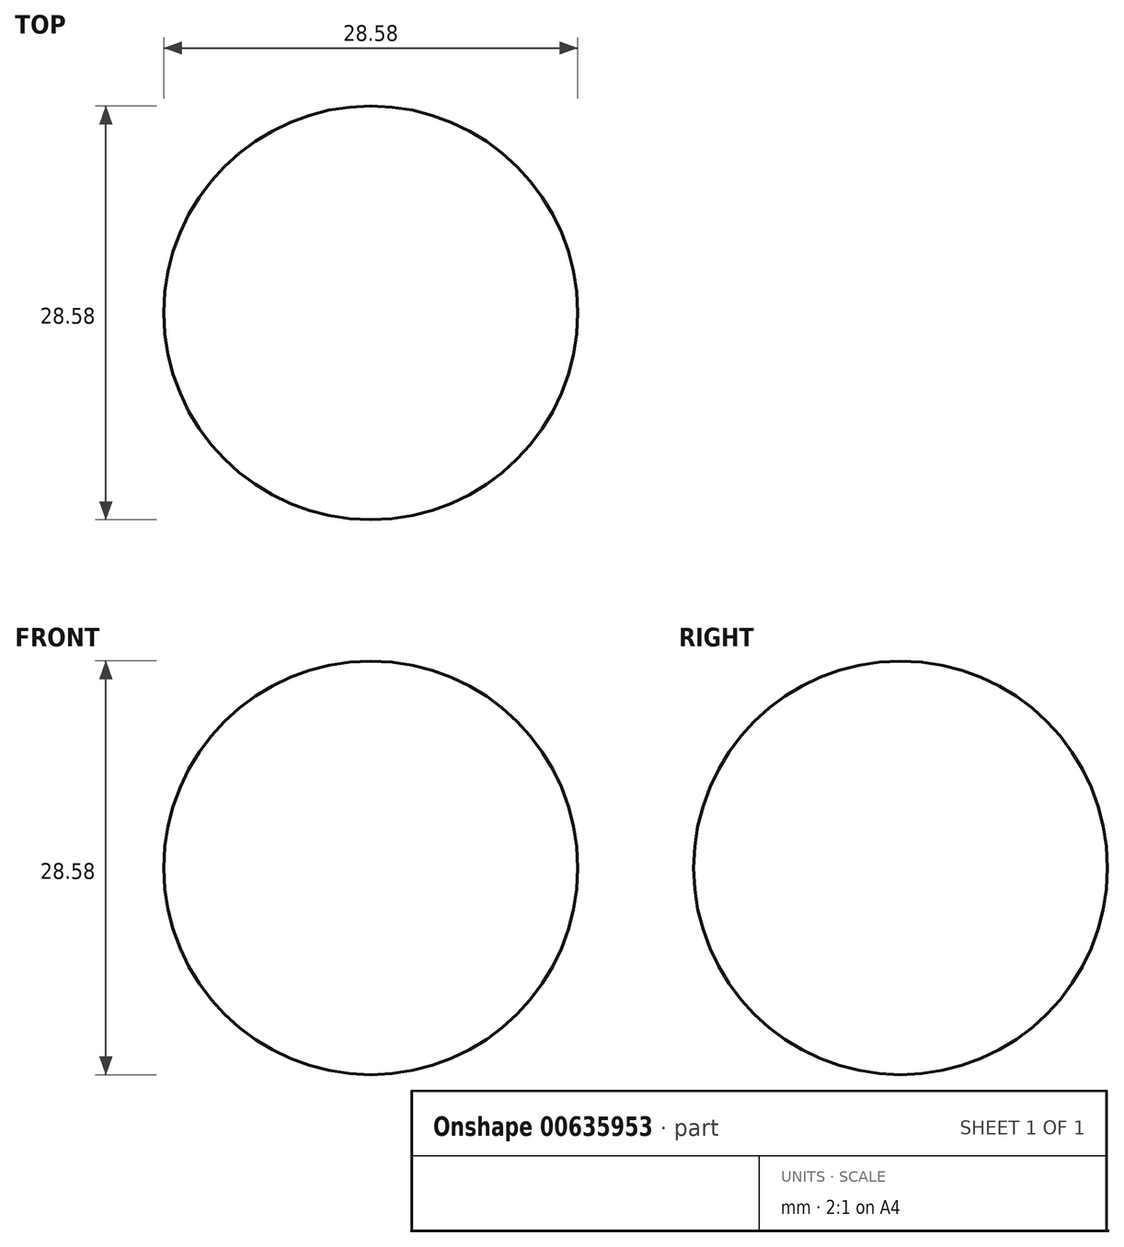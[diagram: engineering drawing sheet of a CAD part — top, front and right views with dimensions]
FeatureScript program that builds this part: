
annotation { "Feature Type Name" : "Feature", "Feature Type Description" : "" }
export const myFeature = defineFeature(function(context is Context, id is Id, definition is map)
    precondition{}
    {
        {
            var Q0;
            Q0=qCreatedBy(makeId("Front.planeOp"),FACE);
            var sketch = newSketch(context, id + "F0", { "sketchPlane" : qUnion([Q0])});
            skArc(sketch, "E0", {"start": v(0, 14.29) * mm, "mid": v(-14.29, 0) * mm, "end": v(0, -14.29) * mm});
            skLineSegment(sketch, "E1", {"start": v(0, 14.29) * mm, "end": v(0, -14.29) * mm});
            skSolve(sketch);
        }
        {
            var Q0;
            Q0=makeQuery(id+"F0.imprint","IMPRINT",FACE,{"disambiguationData":[TD([[makeQuery(id+"F0.imprint","IMPRINT",EDGE,{"derivedFrom":sQuery(id+"F0.wireOp",EDGE,"E0")}),1.0]])]});
            var Q1;
            Q1=sQuery(id+"F0.wireOp",EDGE,"E1");
            revolve(context, id + "F1", {"entities" : qUnion([Q0]), "axis" : qUnion([Q1]), "revolveType" : RevolveType.FULL});
        }
    });
